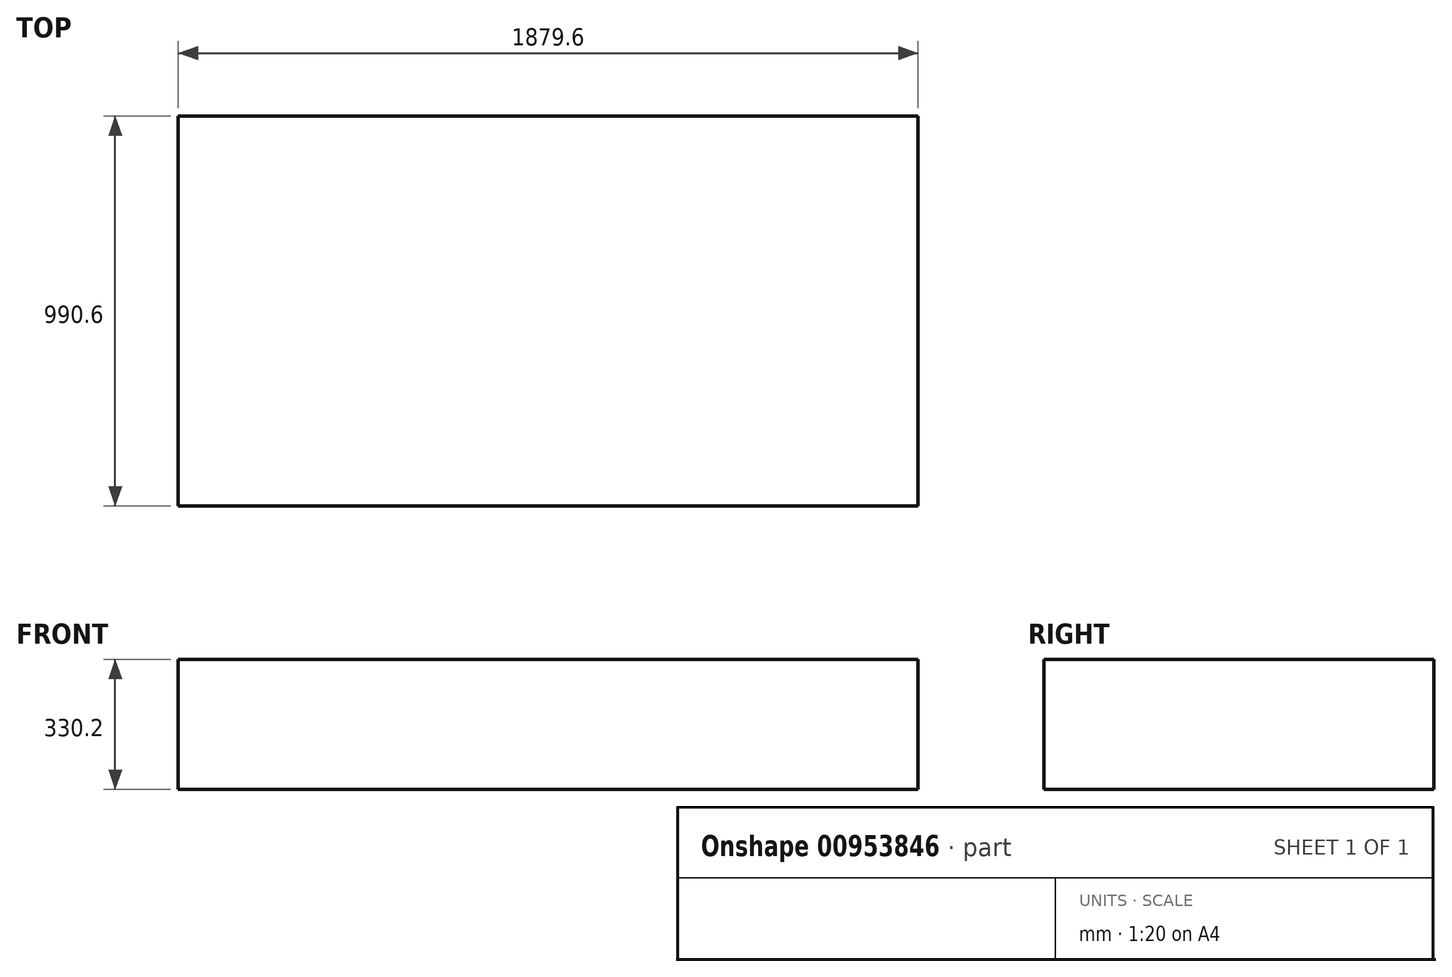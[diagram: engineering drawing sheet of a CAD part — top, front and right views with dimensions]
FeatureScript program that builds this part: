
annotation { "Feature Type Name" : "Feature", "Feature Type Description" : "" }
export const myFeature = defineFeature(function(context is Context, id is Id, definition is map)
    precondition{}
    {
        {
            var Q0;
            Q0=qCreatedBy(makeId("Top.planeOp"),FACE);
            var sketch = newSketch(context, id + "F0", { "sketchPlane" : qUnion([Q0])});
            skLineSegment(sketch, "E0.bottom", {"start": v(-939.8, -495.3) * mm, "end": v(939.8, -495.3) * mm});
            skLineSegment(sketch, "E0.top", {"start": v(-939.8, 495.3) * mm, "end": v(939.8, 495.3) * mm});
            skLineSegment(sketch, "E0.left", {"start": v(-939.8, -495.3) * mm, "end": v(-939.8, 495.3) * mm});
            skLineSegment(sketch, "E0.right", {"start": v(939.8, -495.3) * mm, "end": v(939.8, 495.3) * mm});
            skPoint(sketch, "E0.middle", {"position": v(0, 0) * mm});
            skSolve(sketch);
        }
        {
            var Q0;
            Q0 = qSketchRegion(id + "F0", true);
            extrude(context, id + "F1", {"entities" : qUnion([Q0]), "depth" : 165.1 * mm, "offsetDistance" : 25.4 * mm, "hasSecondDirection" : true, "secondDirectionOppositeDirection" : true, "secondDirectionDepth" : 165.1 * mm});
        }
    });
